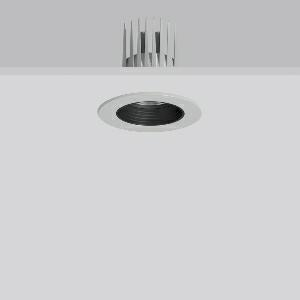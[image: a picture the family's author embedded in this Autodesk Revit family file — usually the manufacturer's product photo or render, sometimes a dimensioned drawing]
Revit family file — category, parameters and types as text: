
# Revit family: heledon_mini_e_901743_004_1_fc4b
name_source: partatom
category: Lighting Fixtures
units: mm (PartAtom-declared; Revit-internal decimal feet)

## family parameters
Cut with Voids When Loaded = No
Host = Face
Light Source = No
Part Type = Normal
Room Calculation Point = No
Round Connector Dimension = Use Diameter
Shared = No

## types (1)
- HELEDON mini E (1 x LED Modul 940, 2400 lm, 4000)
    Apparent Load = 20 VA
    Approval mark = CE
    CIE Flux Codes = 99 100 100 100 100
    Color Rendering = 92
    Color Temperature = 4000
    Default Elevation = 1800 mm
    Description = Series: HELEDON mini
Round recessed downlight. Housing: die-cast aluminium, powder-coated. Black plastic ring and recessed LED to prevent glare from the side. Optical assembly with lens made of plastic (polycarbonate) for the best homogeneous light distribution - can be changed without tools. Best colour rendering index Ra>90. Suitable for Recessed ceiling mounting. Installation without tools thanks to spring fastening system. Including separate LED converter with connecting cable 600 mm.High quality converter without flickering and stroboscopic effect. Through-wiring box (5 pole) available as accessory. The following accessories can be mounted without use of tools: interchangeable lenses, decorative glasses, honeycomb louvre, clear and frosted diffusers, white interchangeable plastic ring. 
Colour: silver
Diameter: 124 mm
Height: 3 mm
Cut-out diameter: 114 mm
Recess height: 170 mm
Luminaire: recess height: 120 mm
Lamp: LED
Socket: without socket
Colour temperature: 4000K
Colour rendering index (CRI): 92
System power: 20 W
Rated luminous flux: 2400 lm
Luminous efficiency: 120 lm/W
Control gear: Regulated power supply
Protection class: II
Type of protection: IP 20
    Height = 0 mm  [stored 0 ft]
    Lamp = 1 x LED Modul 940
    Lamp Light Flux = 2400 lm
    Lamp count = 1
    Length = 124 mm  [stored 0.406824 ft]
    Lifetime = 50000 h
    Luminous efficacy = 120 lm/W
    Manufacturer = RZB
    ModVariant = No
    Model = 901743.004.1
    Mounting Place = Ceiling
    Mounting Type = Recessed
    Number of Poles = 1
    OnlyDefault = Yes
    Power Factor = 1
    Product Name = HELEDON mini E
    Product group = Recessed downlights
    ProductGroupID = 402
    Protection Class = Protection class II
    Protection Degree = IP 20
    RLX_Detail_Level = 1
    RLX_Emergency_Light_Flux = 0 lm
    RLX_Emergency_Type = 0
    RLX_Emergency_Type_DB = No
    RlxData = <blob elided: 126045 chars, md5=158249a4>
    Socket = socket
    Standby Power = 0 W
    System Light Flux = 2400 lm
    System Power = 20 W
    Type Comments = Product without accessories
    Type Image = 901656.004.jpg
    URL = http://relux.com
    VarID = ---
    Voltage = 230 V
    Voltage Range = 220-240 V
    Weight = 0.00 kg
    Width = 0 mm  [stored 0 ft]

note: [stored X ft] marks values corroborated as IEEE doubles in the binary element streams (Revit-internal decimal feet)

## geometry (parser evidence)
native form markers: Blend x4, Sweep x10
no freeform markers — native parametric forms only
